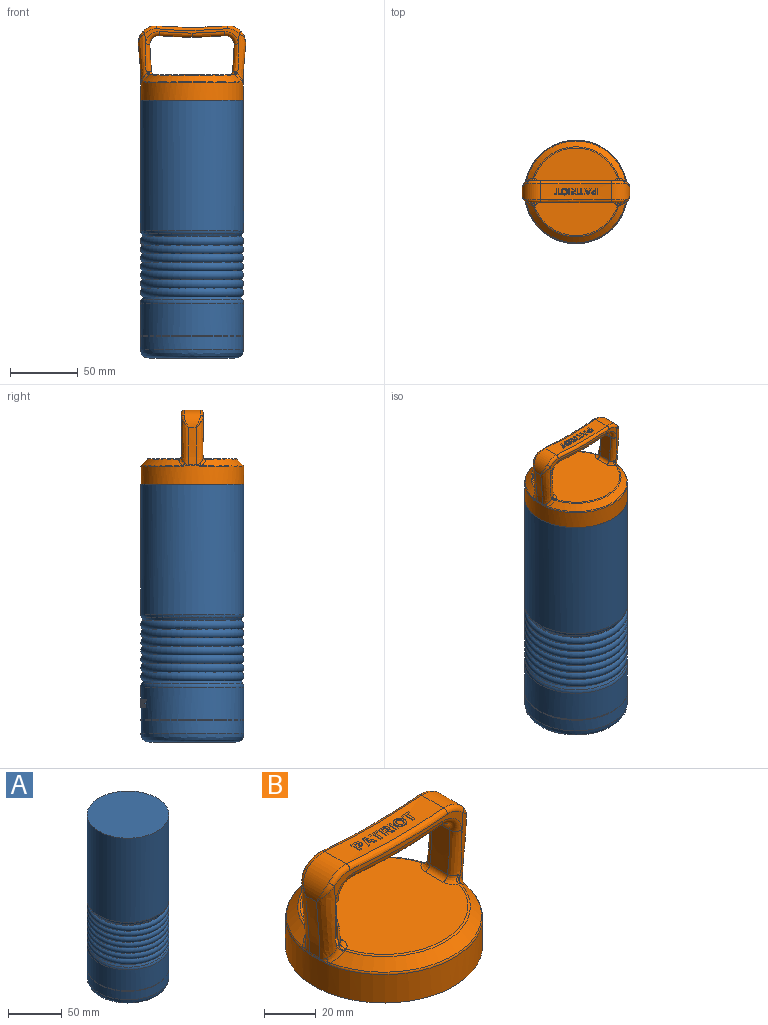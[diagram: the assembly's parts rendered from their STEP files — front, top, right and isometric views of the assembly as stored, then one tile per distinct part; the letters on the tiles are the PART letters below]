
ASSEMBLY  parts=2 mates=1
PART A: 118 faces, bbox 82.5x82.5x190.5 mm
  f0: plane 0.7x0.62mm, normal (0,0,-1), area 0.2mm2, adj f1,f6,f16,f111
  f1: plane 1.83x0.36mm, normal (0.42,0.91,0), area 0.7mm2, adj f0,f2,f16,f111
  f2: plane 0.56x0.55mm, normal (0,0,1), area 0.2mm2, adj f1,f3,f16,f111
  f3: extruded ~0.99x0.75mm, area 0.4mm2, adj f2,f4,f16,f111
  f4: extruded ~0.69x0.49mm, area 0.3mm2, adj f3,f5,f16,f111
  f5: extruded ~0.68x0.47mm, area 0.3mm2, adj f4,f6,f16,f111
  f6: extruded ~0.88x0.7mm, area 0.3mm2, adj f0,f5,f16,f111
  f7: plane 1.93x1.24mm, normal (0,0,1), area 0.8mm2, adj f8,f15,f16,f96
  f8: plane 6.17x0.36mm, normal (-0.42,-0.91,0), area 2.5mm2, adj f7,f9,f16,f96
  f9: plane 1.34x0.96mm, normal (0,0,-1), area 0.5mm2, adj f8,f10,f16,f96
  f10: plane 2.19x0.36mm, normal (0.42,0.91,0), area 0.9mm2, adj f9,f11,f16,f96
  f11: plane 0.67x0.6mm, normal (0,0,-1), area 0.2mm2, adj f10,f12,f16,f96
  f12: extruded ~1.79x1.14mm, area 0.8mm2, adj f11,f13,f16,f96
  f13: extruded ~1.52x0.75mm, area 0.7mm2, adj f12,f14,f16,f96
  f14: extruded ~1.44x0.71mm, area 0.6mm2, adj f13,f15,f16,f96
  f15: extruded ~1.73x1.11mm, area 0.7mm2, adj f7,f14,f16,f96
  f16: cylinder r=38.5mm len=6.17mm, axis (0,0,-1), area 14.9mm2, adj f0,f1,f2,f3,f4,f5,f6,f7
  f17: cylinder r=38.1mm len=1.67mm, axis (0,0,-1), area 2.2mm2, adj f80,f81,f82,f83,f84,f85,f86
  f18: plane 1.35x0.6mm, normal (0,0,1), area 0.5mm2, adj f19,f21,f22,f96
  f19: plane 6.17x0.4mm, normal (0.15,-0.99,0), area 2.5mm2, adj f18,f20,f22,f96
  f20: plane 1.35x0.6mm, normal (0,0,-1), area 0.5mm2, adj f19,f21,f22,f96
  f21: plane 6.17x0.4mm, normal (-0.15,0.99,0), area 2.5mm2, adj f18,f20,f22,f96
  f22: cylinder r=38.5mm len=6.17mm, axis (0,0,-1), area 8.1mm2, adj f18,f19,f20,f21
  f23: extruded ~2.22x1.04mm, area 1mm2, adj f24,f30,f37,f96
  f24: extruded ~2.35x0.85mm, area 1mm2, adj f23,f25,f37,f96
  f25: extruded ~2.36x0.85mm, area 1mm2, adj f24,f26,f37,f96
  f26: extruded ~2.22x1.04mm, area 1mm2, adj f25,f27,f37,f96
  f27: extruded ~2.22x1.04mm, area 1mm2, adj f26,f28,f37,f96
  f28: extruded ~2.36x0.85mm, area 1mm2, adj f27,f29,f37,f96
  f29: extruded ~2.35x0.86mm, area 1mm2, adj f28,f30,f37,f96
  f30: extruded ~2.23x1.04mm, area 1mm2, adj f23,f29,f37,f96
  f31: extruded ~2.08x1.62mm, area 1.2mm2, adj f32,f36,f37,f38
  f32: extruded ~2.08x1.62mm, area 1.2mm2, adj f31,f33,f37,f38
  f33: extruded ~1.24x0.72mm, area 0.5mm2, adj f32,f34,f37,f38
  f34: extruded ~1.56x0.51mm, area 0.7mm2, adj f33,f35,f37,f38
  f35: extruded ~1.56x0.51mm, area 0.7mm2, adj f34,f36,f37,f38
  f36: extruded ~1.25x0.72mm, area 0.5mm2, adj f31,f35,f37,f38
  f37: cylinder r=38.5mm len=6.35mm, axis (0,0,-1), area 19.5mm2, adj f23,f24,f25,f26,f27,f28,f29,f30
  f38: cylinder r=38.1mm len=4.16mm, axis (0,0,-1), area 8.1mm2, adj f31,f32,f33,f34,f35,f36
  f39: plane 1.09x0.36mm, normal (-0.42,0.91,0), area 0.4mm2, adj f40,f46,f47,f96
  f40: plane 4.4x2.32mm, normal (0,0,1), area 1.9mm2, adj f39,f41,f47,f96
  f41: plane 1.09x0.36mm, normal (0.42,-0.91,0), area 0.4mm2, adj f40,f42,f47,f96
  f42: plane 1.72x1.01mm, normal (0,0,-1), area 0.7mm2, adj f41,f43,f47,f96
  f43: plane 5.08x0.36mm, normal (0.42,-0.91,0), area 2mm2, adj f42,f44,f47,f96
  f44: plane 1.36x0.91mm, normal (0,0,-1), area 0.5mm2, adj f43,f45,f47,f96
  f45: plane 5.08x0.36mm, normal (-0.42,0.91,0), area 2mm2, adj f44,f46,f47,f96
  f46: plane 1.66x1.12mm, normal (0,0,-1), area 0.7mm2, adj f39,f45,f47,f96
  f47: cylinder r=38.5mm len=6.17mm, axis (0,0,-1), area 11.7mm2, adj f39,f40,f41,f42,f43,f44,f45,f46
  f48: torus R=34.29mm, axis (0,0,-1), area 1769.3mm2, adj f49,f63
  f49: torus R=34.29mm, axis (0,0,-1), area 1823.2mm2, adj f48,f50
  f50: cone r=38.1mm half-angle=30deg, axis (0,0,-1), area 566.3mm2, adj f49,f65
  f51: plane 76.2x76.2mm, normal (0,0,-1), area 118.9mm2, adj f52,f96
  f52: cylinder r=37.6mm len=75.2mm, axis (0,0,-1), area 118.1mm2, adj f51,f53
  f53: plane 76.2x76.2mm, normal (0,0,1), area 118.9mm2, adj f52,f54
  f54: cylinder r=38.1mm len=76.2mm, axis (0,0,-1), area 2310.1mm2, adj f53,f64
  f55: plane 63.53x63.53mm, normal (0,0,-1), area 3167.3mm2, adj f64
  f56: plane 76.2x76.2mm, normal (0,0,1), area 4560.4mm2, adj f57
  f57: cylinder r=38.1mm len=95.94mm, axis (0,0,-1), area 22967.2mm2, adj f56,f66
  f58: cone r=38.1mm half-angle=30deg, axis (0,0,1), area 566.3mm2, adj f59,f66
  f59: torus R=34.29mm, axis (0,0,-1), area 1823.2mm2, adj f58,f60
  f60: torus R=34.29mm, axis (0,0,-1), area 1769.3mm2, adj f59,f61
  f61: torus R=34.29mm, axis (0,0,-1), area 1769.3mm2, adj f60,f62
  f62: torus R=34.29mm, axis (0,0,-1), area 1769.3mm2, adj f61,f63
  f63: torus R=34.29mm, axis (0,0,-1), area 1769.3mm2, adj f48,f62
  f64: bspline ~76.2x76.2mm, area 2326.9mm2, adj f54,f55
  f65: torus R=33.02mm, axis (0,0,1), area 632.9mm2, adj f50,f96
  f66: torus R=33.02mm, axis (0,0,1), area 632.9mm2, adj f57,f58
  f67: cylinder r=38.5mm len=6.17mm, axis (0,0,-1), area 18.3mm2, adj f68,f69,f70,f71,f72,f73,f74,f75
  f68: plane 2.37x1.49mm, normal (0.03,-0.85,-0.53), area 1.1mm2, adj f67,f69,f79,f96
  f69: plane 0.71x0.41mm, normal (0,0,-1), area 0.3mm2, adj f67,f68,f70,f96
  f70: plane 2.37x0.4mm, normal (-0.03,1,0), area 0.9mm2, adj f67,f69,f71,f96
  f71: plane 1.32x0.42mm, normal (0,0,-1), area 0.5mm2, adj f67,f70,f72,f96
  f72: plane 6.17x0.4mm, normal (0.03,-1,0), area 2.5mm2, adj f67,f71,f73,f96
  f73: plane 1.81x0.42mm, normal (0,0,1), area 0.7mm2, adj f67,f72,f74,f96
  f74: extruded ~1.87x0.48mm, area 0.8mm2, adj f67,f73,f75,f96
  f75: extruded ~1.39x0.62mm, area 0.6mm2, adj f67,f74,f76,f96
  f76: extruded ~0.97x0.42mm, area 0.4mm2, adj f67,f75,f77,f96
  f77: extruded ~0.86x0.66mm, area 0.4mm2, adj f67,f76,f78,f96
  f78: extruded ~2.69x1.83mm, area 1.3mm2, adj f67,f77,f79,f96
  f79: plane 1.46x0.52mm, normal (0,0,-1), area 0.6mm2, adj f67,f68,f78,f96
  f80: extruded ~0.95x0.44mm, area 0.4mm2, adj f17,f67,f81,f86
  f81: extruded ~0.62x0.41mm, area 0.3mm2, adj f17,f67,f80,f82
  f82: extruded ~0.65x0.41mm, area 0.3mm2, adj f17,f67,f81,f83
  f83: extruded ~0.93x0.43mm, area 0.4mm2, adj f17,f67,f82,f84
  f84: plane 0.43x0.4mm, normal (0,0,1), area 0.2mm2, adj f17,f67,f83,f85
  f85: plane 1.67x0.4mm, normal (-0.03,1,0), area 0.7mm2, adj f17,f67,f84,f86
  f86: plane 0.41x0.4mm, normal (0,0,-1), area 0.2mm2, adj f17,f67,f80,f85
  f87: cylinder r=38.5mm len=6.17mm, axis (0,0,-1), area 11.7mm2, adj f88,f89,f90,f91,f92,f93,f94,f95
  f88: plane 1.72x0.54mm, normal (0,0,-1), area 0.7mm2, adj f87,f89,f95,f96
  f89: plane 5.08x0.4mm, normal (0.12,0.99,0), area 2mm2, adj f87,f88,f90,f96
  f90: plane 1.35x0.56mm, normal (0,0,-1), area 0.5mm2, adj f87,f89,f91,f96
  f91: plane 5.08x0.4mm, normal (-0.12,-0.99,0), area 2mm2, adj f87,f90,f92,f96
  f92: plane 1.7x0.67mm, normal (0,0,-1), area 0.7mm2, adj f87,f91,f93,f96
  f93: plane 1.09x0.4mm, normal (-0.12,-0.99,0), area 0.4mm2, adj f87,f92,f94,f96
  f94: plane 4.67x0.98mm, normal (0,0,1), area 1.9mm2, adj f87,f93,f95,f96
  f95: plane 1.09x0.4mm, normal (0.12,0.99,0), area 0.4mm2, adj f87,f88,f94,f96
  f96: cylinder r=38.1mm len=76.2mm, axis (0,0,-1), area 5638mm2, adj f7,f8,f9,f10,f11,f12,f13,f14
  f97: cylinder r=38.1mm len=2.67mm, axis (0,0,-1), area 2.1mm2, adj f99,f100,f101,f102
  f98: cylinder r=38.5mm len=6.19mm, axis (0,0,-1), area 17.3mm2, adj f99,f100,f101,f102,f103,f104,f105,f106
  f99: extruded ~2.67x0.88mm, area 1.1mm2, adj f97,f98,f100,f102
  f100: plane 1.65x0.83mm, normal (0,0,1), area 0.6mm2, adj f97,f98,f99,f101
  f101: extruded ~2.26x0.78mm, area 0.9mm2, adj f97,f98,f100,f102
  f102: extruded ~0.42x0.41mm, area 0.2mm2, adj f97,f98,f99,f101
  f103: plane 1.64x0.83mm, normal (0,0,1), area 0.6mm2, adj f96,f98,f104,f110
  f104: plane 6.2x2.18mm, normal (-0.26,-0.91,0.33), area 2.6mm2, adj f96,f98,f103,f105
  f105: plane 1.44x0.86mm, normal (0,0,-1), area 0.6mm2, adj f96,f98,f104,f106
  f106: plane 1.47x0.53mm, normal (0.26,0.92,-0.29), area 0.6mm2, adj f96,f98,f105,f107
  f107: plane 2.27x1.01mm, normal (0,0,-1), area 0.9mm2, adj f96,f98,f106,f108
  f108: plane 1.47x0.54mm, normal (-0.26,-0.92,-0.29), area 0.6mm2, adj f96,f98,f107,f109
  f109: plane 1.49x0.7mm, normal (0,0,-1), area 0.6mm2, adj f96,f98,f108,f110
  f110: plane 6.2x2.24mm, normal (0.26,0.91,0.33), area 2.6mm2, adj f96,f98,f103,f109
  f111: cylinder r=38.1mm len=1.83mm, axis (0,0,-1), area 2.5mm2, adj f0,f1,f2,f3,f4,f5,f6
  f112: torus R=34.29mm, axis (0,0,-1), area 96.3mm2, adj f113,f114
  f113: cone r=32.59mm half-angle=30deg, axis (0,0,-1), area 85.1mm2, adj f112,f114
  f114: torus R=34.29mm, axis (0,0,-1), area 48mm2, adj f112,f113
  f115: cone r=32.59mm half-angle=30deg, axis (0,0,1), area 85.1mm2, adj f116,f117
  f116: torus R=34.29mm, axis (0,0,-1), area 96.3mm2, adj f115,f117
  f117: torus R=34.29mm, axis (0,0,-1), area 48mm2, adj f115,f116
PART B: 183 faces, bbox 80.7x82.3x68.8 mm
  f0: extruded ~1.34x0.4mm, area 0.4mm2, adj f1,f9,f16,f18
  f1: extruded ~1.12x0.48mm, area 0.4mm2, adj f0,f2,f16,f18
  f2: extruded ~0.83x0.31mm, area 0.3mm2, adj f1,f3,f16,f18
  f3: extruded ~0.62x0.56mm, area 0.3mm2, adj f2,f4,f16,f18
  f4: extruded ~0.95x0.35mm, area 0.3mm2, adj f3,f5,f16,f18
  f5: plane 1.2x0.36mm, normal (0,-1,0), area 0.4mm2, adj f4,f6,f16,f18
  f6: plane 1.69x0.3mm, normal (1,0,-0.05), area 0.5mm2, adj f5,f7,f16,f18
  f7: plane 1.02x0.35mm, normal (0,-1,0), area 0.3mm2, adj f6,f8,f16,f18
  f8: plane 4.79x0.3mm, normal (-1,0,0.05), area 1.4mm2, adj f7,f9,f16,f18
  f9: plane 2.16x0.41mm, normal (0,1,0), area 0.6mm2, adj f0,f8,f16,f18
  f10: plane 1.55x0.3mm, normal (1,0,-0.05), area 0.5mm2, adj f14,f15,f16,f17
  f11: extruded ~0.9x0.75mm, area 0.4mm2, adj f12,f15,f16,f17
  f12: extruded ~0.59x0.31mm, area 0.2mm2, adj f11,f13,f16,f17
  f13: extruded ~0.65x0.33mm, area 0.2mm2, adj f12,f14,f16,f17
  f14: plane 1.08x0.35mm, normal (0,1,0), area 0.3mm2, adj f10,f13,f16,f17
  f15: plane 1.05x0.35mm, normal (0,-1,0), area 0.3mm2, adj f10,f11,f16,f17
  f16: extruded ~4.79x3.93mm, area 10.1mm2, adj f0,f1,f2,f3,f4,f5,f6,f7
  f17: extruded ~1.93x1.55mm, area 2.5mm2, adj f10,f11,f12,f13,f14,f15
  f18: extruded ~53x11.94mm, area 557.8mm2, adj f0,f1,f2,f3,f4,f5,f6,f7
  f19: plane 4.79x1.75mm, normal (0.94,0.34,-0.03), area 1.5mm2, adj f18,f20,f26,f34
  f20: plane 1x0.33mm, normal (0,-1,0), area 0.3mm2, adj f18,f19,f21,f34
  f21: plane 1.22x0.43mm, normal (-0.94,-0.33,0.03), area 0.4mm2, adj f18,f20,f22,f34
  f22: plane 1.83x0.36mm, normal (0,-1,0), area 0.5mm2, adj f18,f21,f23,f34
  f23: plane 1.22x0.43mm, normal (0.94,-0.33,-0.03), area 0.4mm2, adj f18,f22,f24,f34
  f24: plane 1.01x0.34mm, normal (0,-1,0), area 0.3mm2, adj f18,f23,f25,f34
  f25: plane 4.79x1.76mm, normal (-0.94,0.34,0.03), area 1.5mm2, adj f18,f24,f26,f34
  f26: plane 1.19x0.34mm, normal (0,1,0), area 0.4mm2, adj f18,f19,f25,f34
  f27: plane 1.38x0.48mm, normal (-0.95,-0.33,0.03), area 0.4mm2, adj f32,f33,f34,f35
  f28: extruded ~1.72x0.59mm, area 0.5mm2, adj f29,f33,f34,f35
  f29: extruded ~0.3x0.28mm, area 0.1mm2, adj f28,f30,f34,f35
  f30: plane 0.3x0.08mm, normal (0.97,-0.25,-0.03), area 0mm2, adj f29,f31,f34,f35
  f31: plane 0.3x0.24mm, normal (-0.96,-0.29,0.03), area 0.1mm2, adj f30,f32,f34,f35
  f32: plane 0.46x0.3mm, normal (-0.95,-0.3,0.03), area 0.1mm2, adj f27,f31,f34,f35
  f33: plane 1.39x0.34mm, normal (0,1,0), area 0.4mm2, adj f27,f28,f34,f35
  f34: extruded ~4.79x4.67mm, area 9.9mm2, adj f19,f20,f21,f22,f23,f24,f25,f26
  f35: extruded ~2.07x1.38mm, area 1.4mm2, adj f27,f28,f29,f30,f31,f32,f33
  f36: plane 0.77x0.3mm, normal (-1,0,0.01), area 0.2mm2, adj f18,f40,f41,f44
  f37: plane 4.01x0.3mm, normal (-1,0,0.01), area 1.2mm2, adj f18,f41,f42,f44
  f38: plane 4.01x0.3mm, normal (1,0,-0.01), area 1.2mm2, adj f18,f42,f43,f44
  f39: plane 0.77x0.3mm, normal (1,0,-0.01), area 0.2mm2, adj f18,f40,f43,f44
  f40: plane 4.1x0.36mm, normal (0,1,0), area 1.2mm2, adj f18,f36,f39,f44
  f41: plane 1.55x0.33mm, normal (0,-1,0), area 0.5mm2, adj f18,f36,f37,f44
  f42: plane 1.01x0.31mm, normal (0,-1,0), area 0.3mm2, adj f18,f37,f38,f44
  f43: plane 1.55x0.32mm, normal (0,-1,0), area 0.5mm2, adj f18,f38,f39,f44
  f44: extruded ~4.79x4.1mm, area 7.2mm2, adj f36,f37,f38,f39,f40,f41,f42,f43
  f45: plane 2.01x1.3mm, normal (0.84,0.54,0), area 0.7mm2, adj f18,f46,f56,f63
  f46: plane 1.13x0.31mm, normal (0,-1,0), area 0.3mm2, adj f18,f45,f47,f63
  f47: plane 1.82x1.11mm, normal (-0.85,-0.52,0), area 0.6mm2, adj f18,f46,f48,f63
  f48: plane 1.18x0.3mm, normal (0,-1,0), area 0.4mm2, adj f18,f47,f49,f63
  f49: plane 1.82x0.3mm, normal (1,0,0), area 0.5mm2, adj f18,f48,f50,f63
  f50: plane 1x0.3mm, normal (0,-1,0), area 0.3mm2, adj f18,f49,f51,f63
  f51: plane 4.79x0.3mm, normal (-1,0,0), area 1.4mm2, adj f18,f50,f52,f63
  f52: plane 2.39x0.3mm, normal (0,1,0), area 0.7mm2, adj f18,f51,f53,f63
  f53: extruded ~1.32x0.37mm, area 0.4mm2, adj f18,f52,f54,f63
  f54: extruded ~1.06x0.47mm, area 0.4mm2, adj f18,f53,f55,f63
  f55: extruded ~0.87x0.3mm, area 0.3mm2, adj f18,f54,f56,f63
  f56: extruded ~0.77x0.48mm, area 0.3mm2, adj f18,f45,f55,f63
  f57: plane 1.41x0.3mm, normal (1,0,0), area 0.4mm2, adj f61,f62,f63,f64
  f58: extruded ~0.89x0.69mm, area 0.4mm2, adj f59,f62,f63,f64
  f59: extruded ~0.53x0.3mm, area 0.2mm2, adj f58,f60,f63,f64
  f60: extruded ~0.64x0.3mm, area 0.2mm2, adj f59,f61,f63,f64
  f61: plane 1.31x0.3mm, normal (0,1,0), area 0.4mm2, adj f57,f60,f63,f64
  f62: plane 1.29x0.3mm, normal (0,-1,0), area 0.4mm2, adj f57,f58,f63,f64
  f63: extruded ~4.79x4.42mm, area 12.3mm2, adj f45,f46,f47,f48,f49,f50,f51,f52
  f64: extruded ~2.17x1.41mm, area 2.6mm2, adj f57,f58,f59,f60,f61,f62
  f65: plane 4.79x0.3mm, normal (-1,0,-0.02), area 1.4mm2, adj f18,f67,f68,f69
  f66: plane 4.79x0.3mm, normal (1,0,0.02), area 1.4mm2, adj f18,f67,f68,f69
  f67: plane 1.01x0.32mm, normal (0,1,0), area 0.3mm2, adj f18,f65,f66,f69
  f68: plane 1.01x0.32mm, normal (0,-1,0), area 0.3mm2, adj f18,f65,f66,f69
  f69: extruded ~4.79x1mm, area 4.8mm2, adj f65,f66,f67,f68
  f70: extruded ~1.79x0.65mm, area 0.6mm2, adj f18,f71,f78,f87
  f71: extruded ~1.79x0.65mm, area 0.6mm2, adj f18,f70,f72,f87
  f72: extruded ~1.32x0.31mm, area 0.4mm2, adj f18,f71,f73,f87
  f73: extruded ~0.87x0.86mm, area 0.4mm2, adj f18,f72,f74,f87
  f74: extruded ~1.29x0.34mm, area 0.4mm2, adj f18,f73,f75,f87
  f75: extruded ~1.78x0.66mm, area 0.6mm2, adj f18,f74,f76,f87
  f76: extruded ~1.82x0.65mm, area 0.6mm2, adj f18,f75,f77,f87
  f77: extruded ~1.8x0.65mm, area 0.6mm2, adj f18,f76,f78,f87
  f78: extruded ~1.79x0.65mm, area 0.6mm2, adj f18,f70,f77,f87
  f79: extruded ~1.03x0.45mm, area 0.3mm2, adj f80,f86,f87,f88
  f80: extruded ~1.24x0.38mm, area 0.4mm2, adj f79,f81,f87,f88
  f81: extruded ~1.22x0.38mm, area 0.4mm2, adj f80,f82,f87,f88
  f82: extruded ~1.05x0.44mm, area 0.3mm2, adj f81,f83,f87,f88
  f83: extruded ~1.04x0.44mm, area 0.3mm2, adj f82,f84,f87,f88
  f84: extruded ~1.22x0.38mm, area 0.4mm2, adj f83,f85,f87,f88
  f85: extruded ~1.25x0.37mm, area 0.4mm2, adj f84,f86,f87,f88
  f86: extruded ~1.05x0.44mm, area 0.4mm2, adj f79,f85,f87,f88
  f87: extruded ~4.93x4.83mm, area 10.8mm2, adj f70,f71,f72,f73,f74,f75,f76,f77
  f88: extruded ~3.35x2.8mm, area 6.9mm2, adj f79,f80,f81,f82,f83,f84,f85,f86
  f89: plane 0.77x0.3mm, normal (-1,0,-0.05), area 0.2mm2, adj f18,f93,f94,f97
  f90: plane 4.01x0.3mm, normal (-1,0,-0.05), area 1.2mm2, adj f18,f94,f95,f97
  f91: plane 4.01x0.3mm, normal (1,0,0.05), area 1.2mm2, adj f18,f95,f96,f97
  f92: plane 0.77x0.3mm, normal (1,0,0.05), area 0.2mm2, adj f18,f93,f96,f97
  f93: plane 4.11x0.5mm, normal (0,1,0), area 1.2mm2, adj f18,f89,f92,f97
  f94: plane 1.56x0.37mm, normal (0,-1,0), area 0.5mm2, adj f18,f89,f90,f97
  f95: plane 1.02x0.35mm, normal (0,-1,0), area 0.3mm2, adj f18,f90,f91,f97
  f96: plane 1.56x0.38mm, normal (0,-1,0), area 0.5mm2, adj f18,f91,f92,f97
  f97: extruded ~4.79x4.09mm, area 7.2mm2, adj f89,f90,f91,f92,f93,f94,f95,f96
  f98: cone r=32.92mm half-angle=45deg, axis (0,0,-1), area 569.9mm2, adj f138,f140,f141,f143,f167,f168,f169,f176
  f99: extruded ~27.76x5.84mm, area 162.6mm2, adj f112,f127,f129,f134
  f100: extruded ~27.76x5.84mm, area 162.6mm2, adj f111,f126,f128,f144
  f101: plane 69.59x17.68mm, normal (0,-1,0), area 168.7mm2, adj f120,f121,f122,f123,f124,f125,f128,f129
  f102: plane 69.59x17.68mm, normal (0,1,0), area 168.7mm2, adj f114,f115,f116,f117,f118,f119,f126,f127
  f103: cylinder r=38mm len=76mm, axis (0,0,1), area 3205.8mm2, adj f104,f171,f172,f173,f174,f175,f176,f177
  f104: plane 76x76mm, normal (0,0,-1), area 4536.5mm2, adj f103
  f105: extruded ~20.37x9.65mm, area 197.1mm2, adj f107,f114,f120,f137
  f106: extruded ~20.37x9.65mm, area 197.1mm2, adj f110,f119,f125,f147
  f107: cylinder r=6.35mm len=9.65mm, axis (0,1,0), area 98.3mm2, adj f105,f108,f115,f121
  f108: extruded ~24.36x9.65mm, area 235.4mm2, adj f107,f109,f116,f122
  f109: extruded ~24.36x9.65mm, area 235.4mm2, adj f108,f110,f117,f123
  f110: cylinder r=6.35mm len=9.65mm, axis (0,1,0), area 98.3mm2, adj f106,f109,f118,f124
  f111: cylinder r=12.7mm len=13.25mm, axis (0,1,0), area 217.2mm2, adj f18,f100,f154,f155,f159,f160
  f112: cylinder r=12.7mm len=13.25mm, axis (0,1,0), area 217.2mm2, adj f18,f99,f151,f152,f156,f157
  f113: plane 64.79x61.59mm, normal (0,0,1), area 3134.2mm2, adj f135,f137,f139,f145,f147,f149,f163,f168
  f114: bspline ~21.63x4.6mm, area 101.9mm2, adj f102,f105,f115,f127,f131,f133,f135
  f115: torus R=9.53mm, axis (0,-1,0), area 60.1mm2, adj f102,f107,f114,f116
  f116: bspline ~31.59x4.77mm, area 121.3mm2, adj f102,f108,f115,f117
  f117: bspline ~35.91x4.77mm, area 121.3mm2, adj f102,f109,f116,f118
  f118: torus R=9.53mm, axis (0,-1,0), area 60.1mm2, adj f102,f110,f117,f119
  f119: bspline ~21.66x4.9mm, area 104.8mm2, adj f102,f106,f118,f126,f149,f150
  f120: bspline ~21.63x4.6mm, area 101.9mm2, adj f101,f105,f121,f129,f138,f139,f140
  f121: torus R=9.53mm, axis (0,-1,0), area 60.1mm2, adj f101,f107,f120,f122
  f122: bspline ~27.27x4.47mm, area 121.3mm2, adj f101,f108,f121,f123
  f123: bspline ~31.59x4.77mm, area 121.3mm2, adj f101,f109,f122,f124
  f124: torus R=9.53mm, axis (0,-1,0), area 60.1mm2, adj f101,f110,f123,f125
  f125: bspline ~21.63x4.6mm, area 101.9mm2, adj f101,f106,f124,f128,f141,f143,f145
  f126: bspline ~55.22x7.52mm, area 225.6mm2, adj f100,f102,f119,f146,f148,f155
  f127: bspline ~45.78x7.36mm, area 225.7mm2, adj f99,f102,f114,f131,f132,f151
  f128: bspline ~45.78x7.36mm, area 225.7mm2, adj f100,f101,f125,f141,f142,f160
  f129: bspline ~55.22x7.52mm, area 225.6mm2, adj f99,f101,f120,f136,f138,f156
  f130: cone r=32.92mm half-angle=45deg, axis (0,0,-1), area 569.9mm2, adj f131,f133,f148,f150,f162,f163,f164,f177
  f131: bspline ~7.15x6.41mm, area 18mm2, adj f114,f127,f130,f132,f133,f179
  f132: bspline ~4.24x1.86mm, area 2.6mm2, adj f127,f131,f134,f181
  f133: bspline ~4.26x3.74mm, area 2.1mm2, adj f114,f130,f131,f161
  f134: bspline ~6.03x0.86mm, area 3.9mm2, adj f99,f132,f136,f182
  f135: bspline ~6.52x5.74mm, area 18.3mm2, adj f113,f114,f137,f161,f162
  f136: bspline ~4.24x1.86mm, area 2.6mm2, adj f129,f134,f138,f180
  f137: cylinder r=2.54mm len=9.65mm, axis (0,1,0), area 36mm2, adj f105,f113,f135,f139
  f138: bspline ~7.15x6.41mm, area 18mm2, adj f98,f120,f129,f136,f140,f178
  f139: bspline ~6.52x5.74mm, area 18.3mm2, adj f113,f120,f137,f169,f170
  f140: bspline ~4.32x3.76mm, area 2.1mm2, adj f98,f120,f138,f170
  f141: bspline ~7.15x6.41mm, area 18mm2, adj f98,f125,f128,f142,f143,f174
  f142: bspline ~4.24x1.86mm, area 2.6mm2, adj f128,f141,f144,f172
  f143: bspline ~4.26x3.74mm, area 2.1mm2, adj f98,f125,f141,f166
  f144: bspline ~6.03x0.86mm, area 3.9mm2, adj f100,f142,f146,f171
  f145: bspline ~6.52x5.74mm, area 18.3mm2, adj f113,f125,f147,f166,f167
  f146: bspline ~4.24x1.86mm, area 2.6mm2, adj f126,f144,f148,f173
  f147: cylinder r=2.54mm len=9.65mm, axis (0,1,0), area 36mm2, adj f106,f113,f145,f149
  f148: bspline ~7.15x6.41mm, area 17.9mm2, adj f126,f130,f146,f150,f175
  f149: bspline ~6.52x5.74mm, area 18.3mm2, adj f113,f119,f147,f164,f165
  f150: bspline ~4.32x3.76mm, area 2.1mm2, adj f119,f130,f148,f165
  f151: bspline ~10.08x6.2mm, area 11.9mm2, adj f112,f127,f152
  f152: torus R=10.67mm, axis (0,-1,0), area 32.6mm2, adj f102,f112,f151,f153
  f153: bspline ~64.17x4.09mm, area 169.7mm2, adj f18,f102,f152,f154
  f154: torus R=10.67mm, axis (0,-1,0), area 32.6mm2, adj f102,f111,f153,f155
  f155: bspline ~10.08x6.2mm, area 11.8mm2, adj f111,f126,f154
  f156: bspline ~10.08x6.2mm, area 11.8mm2, adj f112,f129,f157
  f157: torus R=10.67mm, axis (0,-1,0), area 32.6mm2, adj f101,f112,f156,f158
  f158: bspline ~64.17x4.13mm, area 169.7mm2, adj f18,f101,f157,f159
  f159: torus R=10.67mm, axis (0,-1,0), area 32.6mm2, adj f101,f111,f158,f160
  f160: bspline ~10.08x6.2mm, area 11.9mm2, adj f111,f128,f159
  f161: bspline ~2.87x2.6mm, area 3.2mm2, adj f133,f135,f162
  f162: bspline ~1.69x1.19mm, area 0.3mm2, adj f130,f135,f161,f163
  f163: torus R=32.39mm, axis (0,0,-1), area 82.3mm2, adj f113,f130,f162,f164
  f164: bspline ~1.69x1.19mm, area 0.3mm2, adj f130,f149,f163,f165
  f165: bspline ~2.87x2.6mm, area 3.2mm2, adj f149,f150,f164
  f166: bspline ~2.86x2.03mm, area 3.3mm2, adj f143,f145,f167
  f167: bspline ~1.69x1.19mm, area 0.3mm2, adj f98,f145,f166,f168
  f168: torus R=32.39mm, axis (0,0,-1), area 82.3mm2, adj f98,f113,f167,f169
  f169: bspline ~1.29x1.07mm, area 0.3mm2, adj f98,f139,f168,f170
  f170: bspline ~2.87x2.6mm, area 3.2mm2, adj f139,f140,f169
  f171: bspline ~5.84x0.4mm, area 2mm2, adj f103,f144,f172,f173
  f172: bspline ~4.75x0.96mm, area 1.4mm2, adj f103,f142,f171,f174
  f173: bspline ~4.77x0.92mm, area 1.4mm2, adj f103,f146,f171,f175
  f174: bspline ~2.89x1.2mm, area 1mm2, adj f103,f141,f172,f176
  f175: bspline ~2.9x1.2mm, area 1mm2, adj f103,f148,f173,f177
  f176: torus R=36.73mm, axis (0,0,1), area 103.9mm2, adj f98,f103,f174,f178
  f177: torus R=36.73mm, axis (0,0,1), area 103.9mm2, adj f103,f130,f175,f179
  f178: bspline ~2.9x1.2mm, area 1mm2, adj f103,f138,f176,f180
  f179: bspline ~2.89x1.2mm, area 1mm2, adj f103,f131,f177,f181
  f180: bspline ~4.77x0.92mm, area 1.4mm2, adj f103,f136,f178,f182
  f181: bspline ~4.75x0.96mm, area 1.4mm2, adj f103,f132,f179,f182
  f182: bspline ~5.84x0.4mm, area 2mm2, adj f103,f134,f180,f181
PLACE A rot(axis=(0,0,1),90deg) t=(-15.41,40.06,-21.76)mm
PLACE B rot(axis=(0,0,-1),180deg) t=(-15.41,40.06,178.24)mm
MATE cylindrical B.f98 <-> A.f16  axis (0,0,-1) through (-15.41,40.06,168.74)mm
